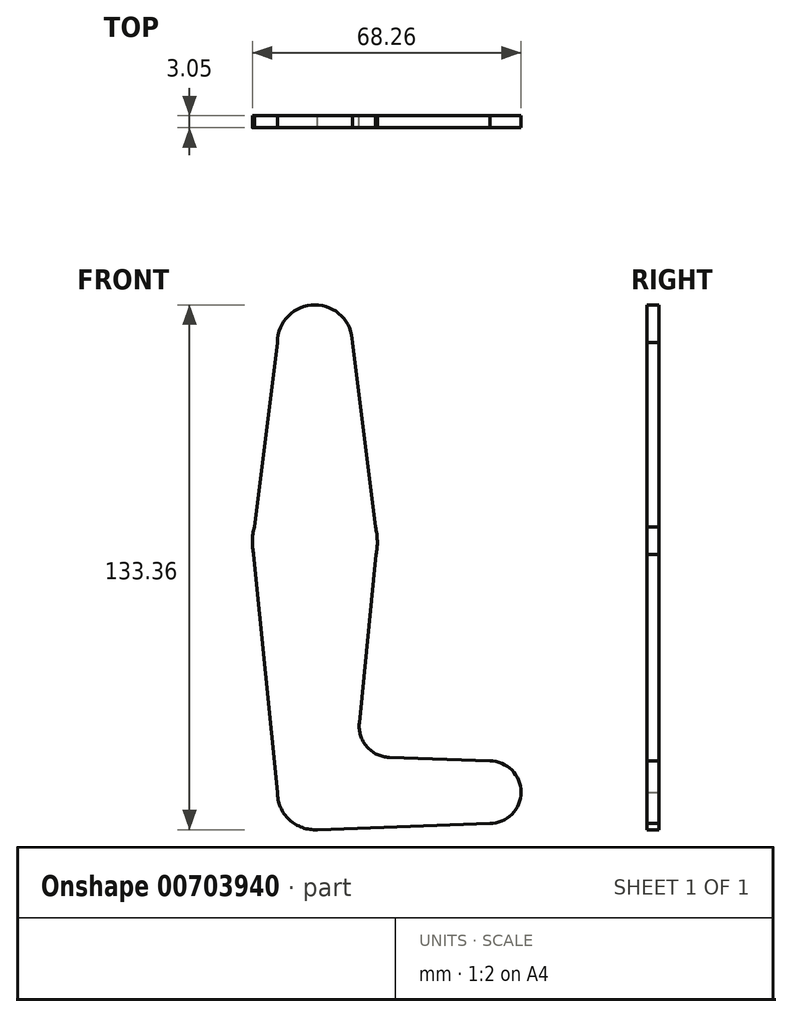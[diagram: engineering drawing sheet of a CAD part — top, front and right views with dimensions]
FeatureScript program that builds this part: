
annotation { "Feature Type Name" : "Feature", "Feature Type Description" : "" }
export const myFeature = defineFeature(function(context is Context, id is Id, definition is map)
    precondition{}
    {
        {
            var Q0;
            Q0=qCreatedBy(makeId("Front.planeOp"),FACE);
            var sketch = newSketch(context, id + "F0", { "sketchPlane" : qUnion([Q0])});
            skLineSegment(sketch, "E0", {"start": v(0, 114.3) * mm, "end": v(0, 0) * mm, "construction": true});
            skLineSegment(sketch, "E1", {"start": v(0, 0) * mm, "end": v(44.45, 0) * mm});
            skCircle(sketch, "E2", {"center": v(0, 114.3) * mm, "radius": 9.53 * mm});
            skCircle(sketch, "E3", {"center": v(0, 63.5) * mm, "radius": 15.88 * mm});
            skCircle(sketch, "E4", {"center": v(0, 0) * mm, "radius": 9.53 * mm});
            skCircle(sketch, "E5", {"center": v(44.45, 0) * mm, "radius": 7.94 * mm});
            skLineSegment(sketch, "E6", {"start": v(-9.53, 114.3) * mm, "end": v(-15.88, 63.5) * mm});
            skLineSegment(sketch, "E7", {"start": v(-15.88, 63.5) * mm, "end": v(-9.52, 0) * mm});
            skLineSegment(sketch, "E8", {"start": v(0, -9.52) * mm, "end": v(44.45, -7.94) * mm});
            skLineSegment(sketch, "E9", {"start": v(9.52, 114.3) * mm, "end": v(15.88, 63.5) * mm});
            skLineSegment(sketch, "E10", {"start": v(15.88, 63.5) * mm, "end": v(11.28, 17.59) * mm});
            skLineSegment(sketch, "E11", {"start": v(18.91, 8.85) * mm, "end": v(44.45, 7.94) * mm});
            skArc(sketch, "E12.filletArc", {"start": v(11.28, 17.59) * mm, "mid": v(13.2, 11.57) * mm, "end": v(18.91, 8.85) * mm});
            skSolve(sketch);
        }
        {
            var Q0;
            Q0 = qSketchRegion(id + "F0", true);
            extrude(context, id + "F1", {"entities" : qUnion([Q0]), "depth" : 3.05 * mm, "offsetDistance" : 25.4 * mm});
        }
    });
